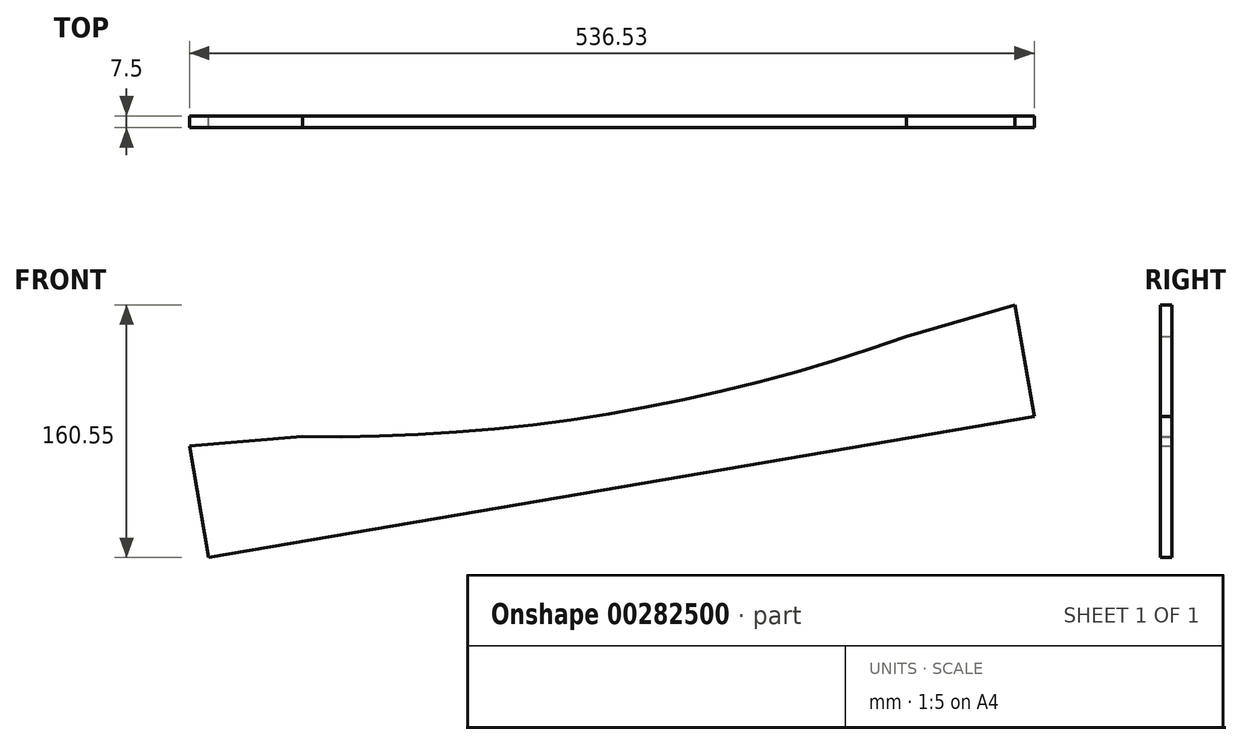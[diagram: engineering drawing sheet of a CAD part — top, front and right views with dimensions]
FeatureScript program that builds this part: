
annotation { "Feature Type Name" : "Feature", "Feature Type Description" : "" }
export const myFeature = defineFeature(function(context is Context, id is Id, definition is map)
    precondition{}
    {
        {
            var Q0;
            Q0=qCreatedBy(makeId("Front.planeOp"),FACE);
            var sketch = newSketch(context, id + "F0", { "sketchPlane" : qUnion([Q0])});
            skLineSegment(sketch, "E0", {"start": v(-1153.84, 13.14) * mm, "end": v(-621.84, 13.14) * mm});
            skLineSegment(sketch, "E1", {"start": v(-1153.84, 13.14) * mm, "end": v(-1153.84, 85.14) * mm});
            skLineSegment(sketch, "E2", {"start": v(-621.84, 13.14) * mm, "end": v(-621.84, 85.14) * mm});
            skLineSegment(sketch, "E3", {"start": v(-621.98, 84.65) * mm, "end": v(-693.75, 78.9) * mm});
            skArc(sketch, "E4", {"start": v(-1082.05, 79.68) * mm, "mid": v(-887.94, 59.25) * mm, "end": v(-693.75, 78.9) * mm});
            skLineSegment(sketch, "E5", {"start": v(-1153.84, 85.14) * mm, "end": v(-1153.84, 13.14) * mm});
            skLineSegment(sketch, "E6", {"start": v(-1153.84, 85.14) * mm, "end": v(-1082.05, 79.68) * mm});
            skLineSegment(sketch, "E7", {"start": v(-1025.7, -395.16) * mm, "end": v(-501.3, -305.59) * mm});
            skLineSegment(sketch, "E8", {"start": v(-501.3, -305.59) * mm, "end": v(-513.42, -234.61) * mm});
            skLineSegment(sketch, "E9", {"start": v(-1025.7, -395.16) * mm, "end": v(-1037.83, -324.18) * mm});
            skLineSegment(sketch, "E10", {"start": v(-1037.83, -324.18) * mm, "end": v(-966.07, -318.33) * mm});
            skLineSegment(sketch, "E11", {"start": v(-513.42, -234.61) * mm, "end": v(-582.57, -254.67) * mm});
            skArc(sketch, "E12", {"start": v(-966.07, -318.33) * mm, "mid": v(-771.44, -303.87) * mm, "end": v(-582.57, -254.67) * mm});
            skSolve(sketch);
        }
        {
            var Q0;
            Q0=makeQuery(id+"F0.imprint","IMPRINT",FACE,{"disambiguationData":[TD([[makeQuery(id+"F0.imprint","IMPRINT",EDGE,{"derivedFrom":sQuery(id+"F0.wireOp",EDGE,"E7")}),1.0]])]});
            extrude(context, id + "F1", {"entities" : qUnion([Q0]), "depth" : 7.5 * mm});
        }
    });
